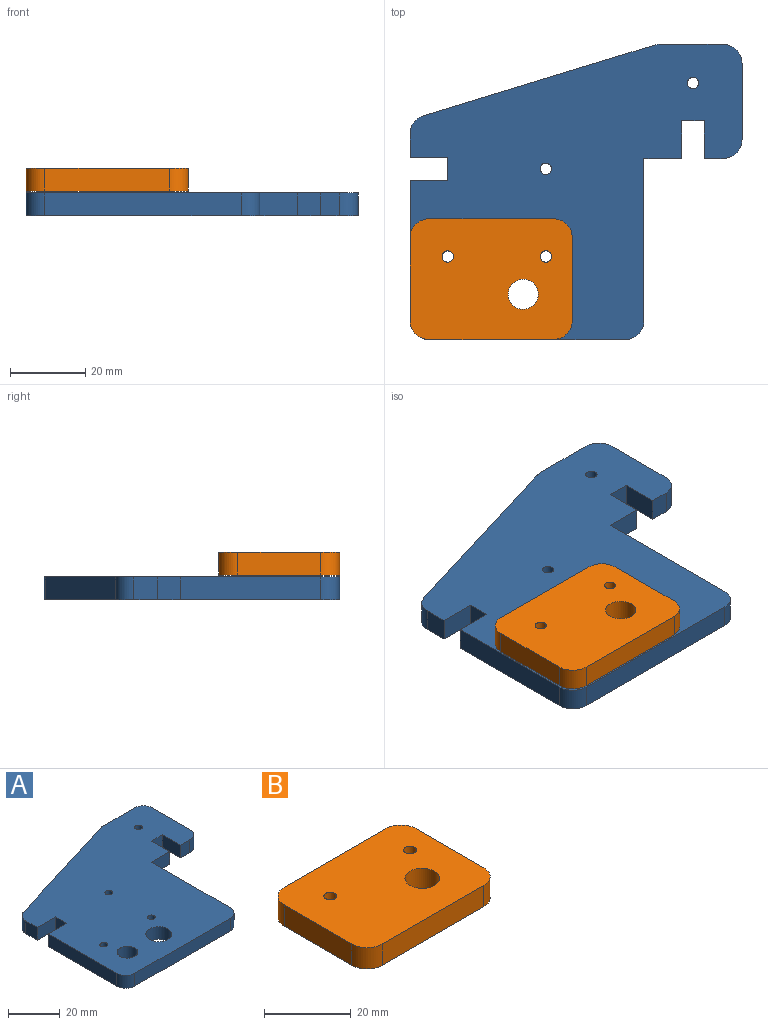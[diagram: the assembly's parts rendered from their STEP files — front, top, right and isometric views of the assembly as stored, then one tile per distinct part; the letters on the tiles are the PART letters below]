
ASSEMBLY  parts=2 mates=1
PART A: 29 faces, bbox 88x78.2x6 mm
  f0: plane 20.24x6mm, normal (1,0,0), area 121.4mm2, adj f1,f2,f21,f28
  f1: plane 88x78.24mm, normal (0,0,1), area 4681.8mm2, adj f0,f3,f4,f5,f6,f7,f8,f9
  f2: plane 88x78.24mm, normal (0,0,-1), area 4681.8mm2, adj f0,f3,f4,f5,f6,f7,f8,f9
  f3: plane 6x5mm, normal (0,-1,0), area 30mm2, adj f1,f2,f9,f21
  f4: plane 6.3x6mm, normal (-1,0,0), area 37.8mm2, adj f1,f2,f14,f26
  f5: plane 43x6mm, normal (1,0,0), area 258mm2, adj f1,f2,f6,f20
  f6: plane 10x6mm, normal (0,-1,0), area 60mm2, adj f1,f2,f5,f11
  f7: plane 37.24x6mm, normal (-1,0,0), area 223.4mm2, adj f1,f2,f12,f19
  f8: plane 52x6mm, normal (0,-1,0), area 312mm2, adj f1,f2,f19,f20
  f9: plane 10x6mm, normal (-1,0,0), area 60mm2, adj f1,f2,f3,f10
  f10: plane 6x6mm, normal (0,-1,0), area 36mm2, adj f1,f2,f9,f11
  f11: plane 10x6mm, normal (1,0,0), area 60mm2, adj f1,f2,f6,f10
  f12: plane 10x6mm, normal (0,1,0), area 60mm2, adj f1,f2,f7,f13
  f13: plane 6x6mm, normal (-1,0,0), area 36mm2, adj f1,f2,f12,f14
  f14: plane 10x6mm, normal (0,-1,0), area 60mm2, adj f1,f2,f4,f13
  f15: cylinder r=1.5mm len=6mm, axis (0,0,1), area 56.5mm2, adj f1,f2
  f16: cylinder r=1.5mm len=6mm, axis (0,0,1), area 56.5mm2, adj f1,f2
  f17: cylinder r=5mm len=10mm, axis (0,0,1), area 188.5mm2, adj f1,f2
  f18: cylinder r=4mm len=8mm, axis (0,0,1), area 150.8mm2, adj f1,f2
  f19: cylinder r=5mm len=6mm, axis (0,0,-1), area 47.1mm2, adj f1,f2,f7,f8
  f20: cylinder r=5mm len=6mm, axis (0,0,1), area 47.1mm2, adj f1,f2,f5,f8
  f21: cylinder r=5mm len=6mm, axis (0,0,1), area 47.1mm2, adj f0,f1,f2,f3
  f22: cylinder r=1.5mm len=6mm, axis (0,0,1), area 56.5mm2, adj f1,f2
  f23: cylinder r=1.5mm len=6mm, axis (0,0,1), area 56.5mm2, adj f1,f2
  f24: plane 16.85x6mm, normal (0,1,0), area 101.1mm2, adj f1,f2,f27,f28
  f25: plane 61.15x18.7mm, normal (-0.29,0.96,0), area 383.7mm2, adj f1,f2,f26,f27
  f26: cylinder r=5mm len=6mm, axis (0,0,-1), area 38.2mm2, adj f1,f2,f4,f25
  f27: cylinder r=5mm len=6mm, axis (0,0,-1), area 8.9mm2, adj f1,f2,f24,f25
  f28: cylinder r=5mm len=6mm, axis (0,0,1), area 47.1mm2, adj f0,f1,f2,f24
PART B: 13 faces, bbox 43x32x6 mm
  f0: plane 22x6mm, normal (-1,0,0), area 132mm2, adj f4,f5,f9,f12
  f1: plane 33x6mm, normal (0,-1,0), area 198mm2, adj f4,f5,f9,f10
  f2: plane 22x6mm, normal (1,0,0), area 132mm2, adj f4,f5,f10,f11
  f3: plane 33x6mm, normal (0,1,0), area 198mm2, adj f4,f5,f11,f12
  f4: plane 43x32mm, normal (0,0,1), area 1290.1mm2, adj f0,f1,f2,f3,f6,f7,f8,f9
  f5: plane 43x32mm, normal (0,0,-1), area 1290.1mm2, adj f0,f1,f2,f3,f6,f7,f8,f9
  f6: cylinder r=1.5mm len=6mm, axis (0,0,1), area 56.5mm2, adj f4,f5
  f7: cylinder r=4mm len=8mm, axis (0,0,1), area 150.8mm2, adj f4,f5
  f8: cylinder r=1.5mm len=6mm, axis (0,0,1), area 56.5mm2, adj f4,f5
  f9: cylinder r=5mm len=6mm, axis (0,0,-1), area 47.1mm2, adj f0,f1,f4,f5
  f10: cylinder r=5mm len=6mm, axis (0,0,1), area 47.1mm2, adj f1,f2,f4,f5
  f11: cylinder r=5mm len=6mm, axis (0,0,-1), area 47.1mm2, adj f2,f3,f4,f5
  f12: cylinder r=5mm len=6mm, axis (0,0,1), area 47.1mm2, adj f0,f3,f4,f5
PLACE A t=(93.77,-4.26,-1.35)mm
PLACE B t=(7.87,1.25,5.13)mm
MATE slider A.f17 <-> B.f7  axis (0,0,1) through (58.36,-40.5,4.65)mm
